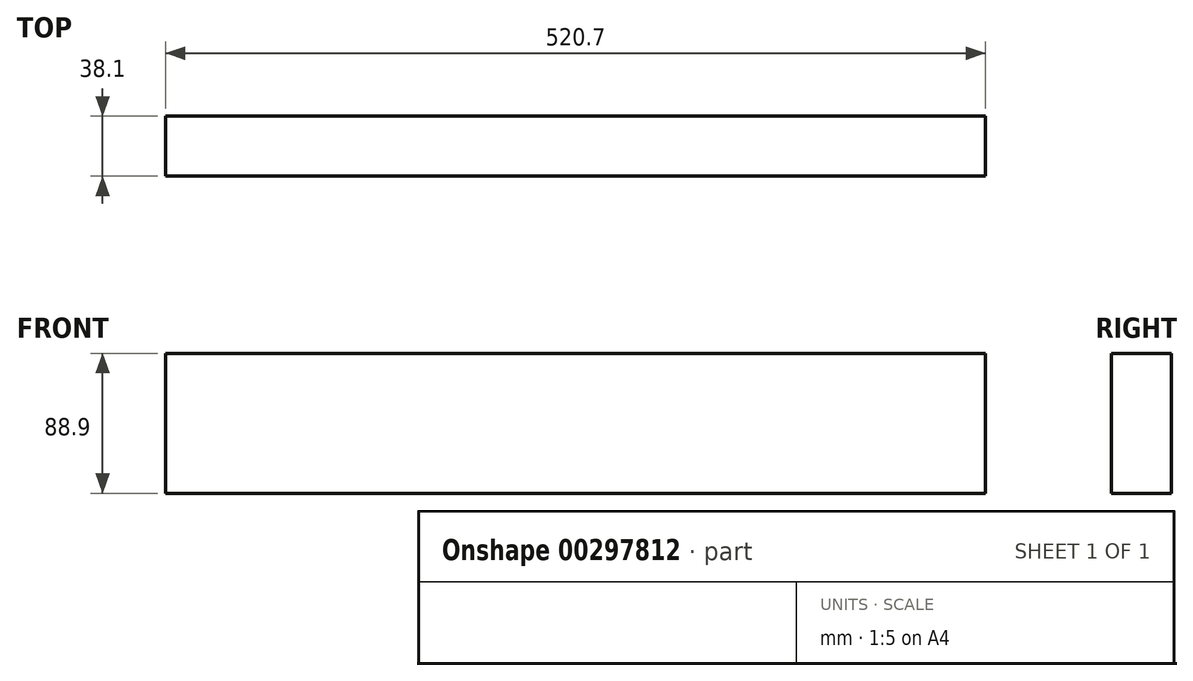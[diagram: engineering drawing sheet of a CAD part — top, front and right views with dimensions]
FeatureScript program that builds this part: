
annotation { "Feature Type Name" : "Feature", "Feature Type Description" : "" }
export const myFeature = defineFeature(function(context is Context, id is Id, definition is map)
    precondition{}
    {
        {
            var Q0;
            Q0=qCreatedBy(makeId("Front.planeOp"),FACE);
            var sketch = newSketch(context, id + "F0", { "sketchPlane" : qUnion([Q0])});
            skLineSegment(sketch, "E0.bottom", {"start": v(0, 0) * mm, "end": v(520.7, 0) * mm});
            skLineSegment(sketch, "E0.top", {"start": v(0, -88.9) * mm, "end": v(520.7, -88.9) * mm});
            skLineSegment(sketch, "E0.left", {"start": v(0, 0) * mm, "end": v(0, -88.9) * mm});
            skLineSegment(sketch, "E0.right", {"start": v(520.7, 0) * mm, "end": v(520.7, -88.9) * mm});
            skSolve(sketch);
        }
        {
            var Q0;
            Q0=makeQuery(id+"F0.imprint","IMPRINT",FACE,{"disambiguationData":[TD([[makeQuery(id+"F0.imprint","IMPRINT",EDGE,{"derivedFrom":sQuery(id+"F0.wireOp",EDGE,"E0.bottom")}),-1.0]])]});
            extrude(context, id + "F1", {"entities" : qUnion([Q0]), "depth" : 38.1 * mm});
        }
    });
